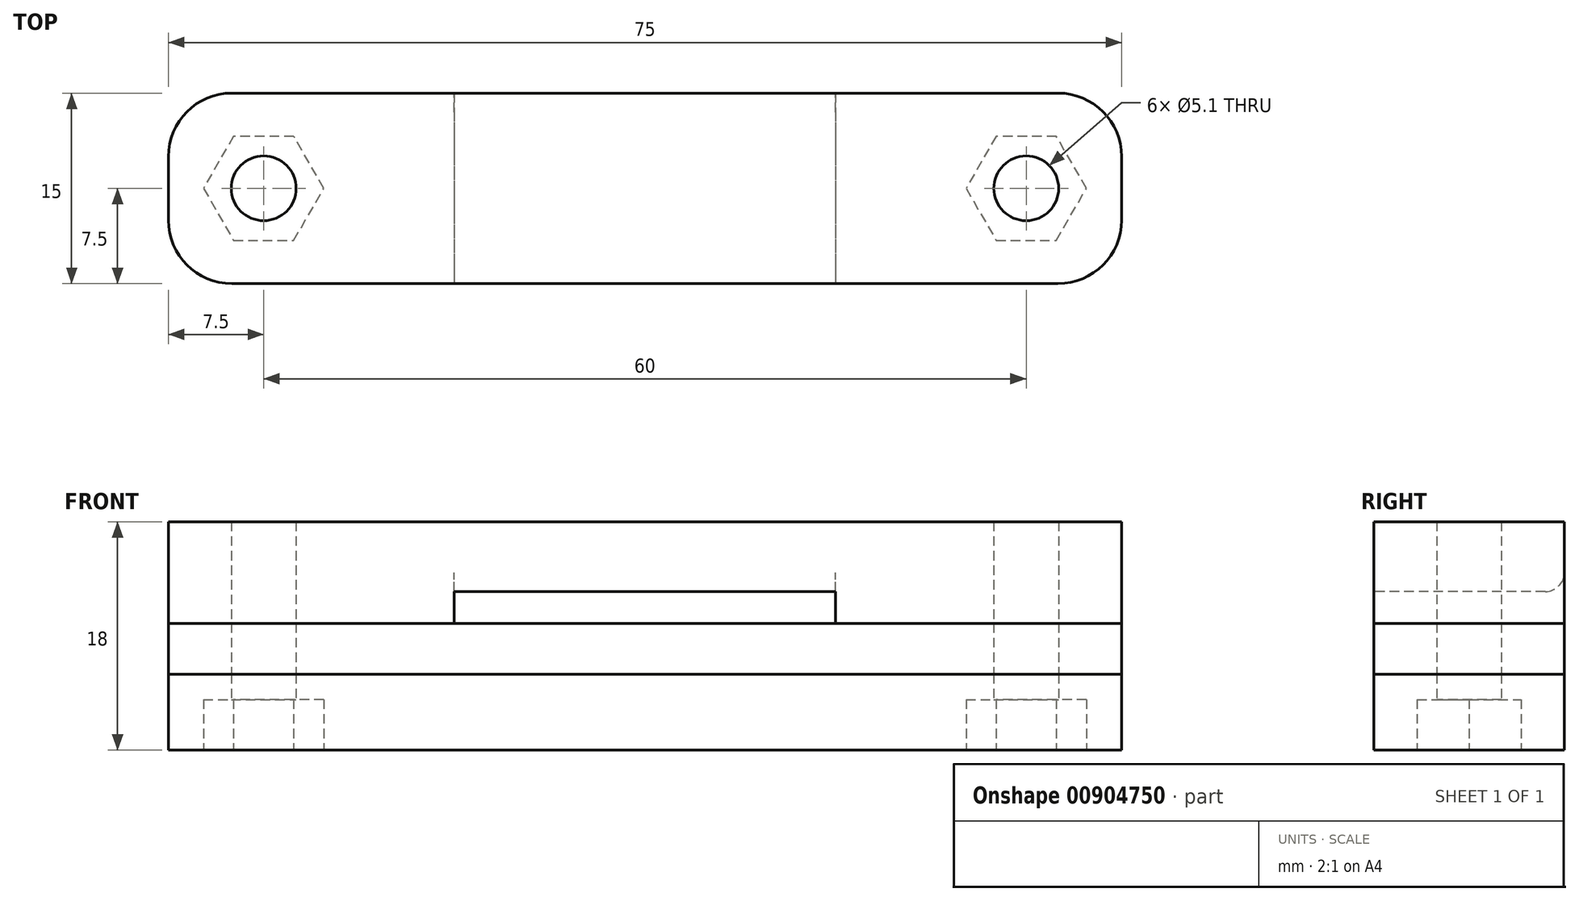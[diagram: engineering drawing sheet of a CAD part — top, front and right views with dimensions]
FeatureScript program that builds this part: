
annotation { "Feature Type Name" : "Feature", "Feature Type Description" : "" }
export const myFeature = defineFeature(function(context is Context, id is Id, definition is map)
    precondition{}
    {
        {
            var Q0;
            Q0=qCreatedBy(makeId("Top.planeOp"),FACE);
            var sketch = newSketch(context, id + "F0", { "sketchPlane" : qUnion([Q0])});
            skLineSegment(sketch, "E0.bottom", {"start": v(32.5, -7.5) * mm, "end": v(-32.5, -7.5) * mm});
            skLineSegment(sketch, "E0.top", {"start": v(32.5, 7.5) * mm, "end": v(-32.5, 7.5) * mm});
            skLineSegment(sketch, "E0.left", {"start": v(37.5, -2.5) * mm, "end": v(37.5, 2.5) * mm});
            skLineSegment(sketch, "E0.right", {"start": v(-37.5, -2.5) * mm, "end": v(-37.5, 2.5) * mm});
            skPoint(sketch, "E0.middle", {"position": v(0, 0) * mm});
            skLineSegment(sketch, "E1", {"start": v(-26.98, 0) * mm, "end": v(-37.5, 0) * mm, "construction": true});
            skLineSegment(sketch, "E2", {"start": v(-37.5, 0) * mm, "end": v(37.5, 0) * mm, "construction": true});
            skCircle(sketch, "E3", {"center": v(-30, 0) * mm, "radius": 2.55 * mm});
            skCircle(sketch, "E4", {"center": v(30, 0) * mm, "radius": 2.55 * mm});
            skLineSegment(sketch, "E5.bottom", {"start": v(25, -3.26) * mm, "end": v(-25, -3.26) * mm, "construction": true});
            skLineSegment(sketch, "E5.top", {"start": v(25, 3.26) * mm, "end": v(-25, 3.26) * mm, "construction": true});
            skLineSegment(sketch, "E5.left", {"start": v(25, -3.26) * mm, "end": v(25, 3.26) * mm, "construction": true});
            skLineSegment(sketch, "E5.right", {"start": v(-25, -3.26) * mm, "end": v(-25, 3.26) * mm, "construction": true});
            skPoint(sketch, "E6.visualSharp", {"position": v(-37.5, 7.5) * mm});
            skArc(sketch, "E6.filletArc", {"start": v(-32.5, 7.5) * mm, "mid": v(-36.04, 6.04) * mm, "end": v(-37.5, 2.5) * mm});
            skPoint(sketch, "E7.visualSharp", {"position": v(-37.5, -7.5) * mm});
            skArc(sketch, "E7.filletArc", {"start": v(-37.5, -2.5) * mm, "mid": v(-36.04, -6.04) * mm, "end": v(-32.5, -7.5) * mm});
            skPoint(sketch, "E8.visualSharp", {"position": v(37.5, -7.5) * mm});
            skArc(sketch, "E8.filletArc", {"start": v(32.5, -7.5) * mm, "mid": v(36.04, -6.04) * mm, "end": v(37.5, -2.5) * mm});
            skPoint(sketch, "E9.visualSharp", {"position": v(37.5, 7.5) * mm});
            skArc(sketch, "E9.filletArc", {"start": v(37.5, 2.5) * mm, "mid": v(36.04, 6.04) * mm, "end": v(32.5, 7.5) * mm});
            skSolve(sketch);
        }
        {
            var Q0;
            Q0=makeQuery(id+"F0.imprint","IMPRINT",FACE,{"disambiguationData":[TD([[makeQuery(id+"F0.imprint","IMPRINT",EDGE,{"derivedFrom":sQuery(id+"F0.wireOp",EDGE,"E0.bottom")}),-1.0]])]});
            extrude(context, id + "F1", {"entities" : qUnion([Q0]), "depth" : 6 * mm, "offsetDistance" : 25 * mm});
        }
        {
            var Q0;
            Q0=makeQuery(id+"F1.opExtrude","CAP_FACE",FACE,{"disambiguationData":[OSD([sQuery(id+"F0.wireOp",EDGE,"E0.bottom"),sQuery(id+"F0.wireOp",EDGE,"E0.top"),sQuery(id+"F0.wireOp",EDGE,"E0.left"),sQuery(id+"F0.wireOp",EDGE,"E0.right"),sQuery(id+"F0.wireOp",EDGE,"E3"),sQuery(id+"F0.wireOp",EDGE,"E4"),sQuery(id+"F0.wireOp",EDGE,"E6.filletArc"),sQuery(id+"F0.wireOp",EDGE,"E7.filletArc"),sQuery(id+"F0.wireOp",EDGE,"E8.filletArc"),sQuery(id+"F0.wireOp",EDGE,"E9.filletArc")])],"isStart":true});
            var sketch = newSketch(context, id + "F2", { "sketchPlane" : qUnion([Q0])});
            skCircle(sketch, "E10.cCircle", {"center": v(-30, 0) * mm, "radius": 4.1 * mm, "construction": true});
            skLineSegment(sketch, "E10.0", {"start": v(-27.63, -4.1) * mm, "end": v(-32.37, -4.1) * mm});
            skLineSegment(sketch, "E10.1", {"start": v(-32.37, -4.1) * mm, "end": v(-34.73, 0) * mm});
            skLineSegment(sketch, "E10.2", {"start": v(-34.73, 0) * mm, "end": v(-32.37, 4.1) * mm});
            skLineSegment(sketch, "E10.3", {"start": v(-32.37, 4.1) * mm, "end": v(-27.63, 4.1) * mm});
            skLineSegment(sketch, "E10.4", {"start": v(-27.63, 4.1) * mm, "end": v(-25.27, 0) * mm});
            skLineSegment(sketch, "E10.5", {"start": v(-25.27, 0) * mm, "end": v(-27.63, -4.1) * mm});
            skPoint(sketch, "E10.0.midPoint", {"position": v(-30, -4.1) * mm});
            skCircle(sketch, "E11.cCircle", {"center": v(30, 0) * mm, "radius": 4.1 * mm, "construction": true});
            skLineSegment(sketch, "E11.0", {"start": v(32.37, -4.1) * mm, "end": v(27.63, -4.1) * mm});
            skLineSegment(sketch, "E11.1", {"start": v(27.63, -4.1) * mm, "end": v(25.27, 0) * mm});
            skLineSegment(sketch, "E11.2", {"start": v(25.27, 0) * mm, "end": v(27.63, 4.1) * mm});
            skLineSegment(sketch, "E11.3", {"start": v(27.63, 4.1) * mm, "end": v(32.37, 4.1) * mm});
            skLineSegment(sketch, "E11.4", {"start": v(32.37, 4.1) * mm, "end": v(34.73, 0) * mm});
            skLineSegment(sketch, "E11.5", {"start": v(34.73, 0) * mm, "end": v(32.37, -4.1) * mm});
            skPoint(sketch, "E11.0.midPoint", {"position": v(30, -4.1) * mm});
            skSolve(sketch);
        }
        {
            var Q0;
            Q0 = qSketchRegion(id + "F2", true);
            extrude(context, id + "F3", {"entities" : qUnion([Q0]), "operationType" : NewBodyOperationType.REMOVE, "oppositeDirection" : true, "depth" : 4 * mm, "offsetDistance" : 25 * mm});
        }
        {
            var Q0;
            Q0=makeQuery(id+"F1.opExtrude","CAP_FACE",FACE,{"disambiguationData":[OSD([sQuery(id+"F0.wireOp",EDGE,"E0.bottom"),sQuery(id+"F0.wireOp",EDGE,"E0.top"),sQuery(id+"F0.wireOp",EDGE,"E0.left"),sQuery(id+"F0.wireOp",EDGE,"E0.right"),sQuery(id+"F0.wireOp",EDGE,"E3"),sQuery(id+"F0.wireOp",EDGE,"E4"),sQuery(id+"F0.wireOp",EDGE,"E6.filletArc"),sQuery(id+"F0.wireOp",EDGE,"E7.filletArc"),sQuery(id+"F0.wireOp",EDGE,"E8.filletArc"),sQuery(id+"F0.wireOp",EDGE,"E9.filletArc")])],"isStart":false});
            var sketch = newSketch(context, id + "F4", { "sketchPlane" : qUnion([Q0])});
            skLineSegment(sketch, "E12.0", {"start": v(32.5, -7.5) * mm, "end": v(-32.5, -7.5) * mm});
            skLineSegment(sketch, "E13.0", {"start": v(32.5, 7.5) * mm, "end": v(-32.5, 7.5) * mm});
            skArc(sketch, "E14.0", {"start": v(37.5, 2.5) * mm, "mid": v(36.04, 6.04) * mm, "end": v(32.5, 7.5) * mm});
            skLineSegment(sketch, "E15.0", {"start": v(37.5, -2.5) * mm, "end": v(37.5, 2.5) * mm});
            skArc(sketch, "E16.0", {"start": v(32.5, -7.5) * mm, "mid": v(36.04, -6.04) * mm, "end": v(37.5, -2.5) * mm});
            skArc(sketch, "E17.0", {"start": v(-37.5, -2.5) * mm, "mid": v(-36.04, -6.04) * mm, "end": v(-32.5, -7.5) * mm});
            skPoint(sketch, "E18.0", {"position": v(-37.5, 2.5) * mm});
            skArc(sketch, "E19.0", {"start": v(-32.5, 7.5) * mm, "mid": v(-36.04, 6.04) * mm, "end": v(-37.5, 2.5) * mm});
            skLineSegment(sketch, "E20.0", {"start": v(-37.5, -2.5) * mm, "end": v(-37.5, 2.5) * mm});
            skCircle(sketch, "E21.0", {"center": v(-30, 0) * mm, "radius": 2.55 * mm});
            skCircle(sketch, "E22.0", {"center": v(30, 0) * mm, "radius": 2.55 * mm});
            skSolve(sketch);
        }
        {
            var Q0;
            Q0 = qSketchRegion(id + "F4", true);
            extrude(context, id + "F5", {"entities" : qUnion([Q0]), "depth" : 4 * mm, "offsetDistance" : 25 * mm});
        }
        {
            var Q0;
            Q0=makeQuery(id+"F5.opExtrude","CAP_FACE",FACE,{"disambiguationData":[OSD([sQuery(id+"F4.wireOp",EDGE,"E12.0"),sQuery(id+"F4.wireOp",EDGE,"E13.0"),sQuery(id+"F4.wireOp",EDGE,"E14.0"),sQuery(id+"F4.wireOp",EDGE,"E15.0"),sQuery(id+"F4.wireOp",EDGE,"E16.0"),sQuery(id+"F4.wireOp",EDGE,"E17.0"),sQuery(id+"F4.wireOp",EDGE,"E19.0"),sQuery(id+"F4.wireOp",EDGE,"E20.0"),sQuery(id+"F4.wireOp",EDGE,"E21.0"),sQuery(id+"F4.wireOp",EDGE,"E22.0")])],"isStart":false});
            var sketch = newSketch(context, id + "F6", { "sketchPlane" : qUnion([Q0])});
            skLineSegment(sketch, "E23.0", {"start": v(32.5, 7.5) * mm, "end": v(-32.5, 7.5) * mm});
            skArc(sketch, "E24.0", {"start": v(37.5, 2.5) * mm, "mid": v(36.04, 6.04) * mm, "end": v(32.5, 7.5) * mm});
            skPoint(sketch, "E25.0", {"position": v(37.5, -2.5) * mm});
            skLineSegment(sketch, "E26.0", {"start": v(37.5, -2.5) * mm, "end": v(37.5, 2.5) * mm});
            skArc(sketch, "E27.0", {"start": v(32.5, -7.5) * mm, "mid": v(36.04, -6.04) * mm, "end": v(37.5, -2.5) * mm});
            skLineSegment(sketch, "E28.0", {"start": v(32.5, -7.5) * mm, "end": v(-32.5, -7.5) * mm});
            skCircle(sketch, "E29.0", {"center": v(30, 0) * mm, "radius": 2.55 * mm});
            skArc(sketch, "E30.0", {"start": v(-32.5, 7.5) * mm, "mid": v(-36.04, 6.04) * mm, "end": v(-37.5, 2.5) * mm});
            skLineSegment(sketch, "E31.0", {"start": v(-37.5, -2.5) * mm, "end": v(-37.5, 2.5) * mm});
            skArc(sketch, "E32.0", {"start": v(-37.5, -2.5) * mm, "mid": v(-36.04, -6.04) * mm, "end": v(-32.5, -7.5) * mm});
            skCircle(sketch, "E33.0", {"center": v(-30, 0) * mm, "radius": 2.55 * mm});
            skSolve(sketch);
        }
        {
            var Q0;
            Q0 = qSketchRegion(id + "F6", true);
            extrude(context, id + "F7", {"entities" : qUnion([Q0]), "depth" : 8 * mm, "offsetDistance" : 25 * mm});
        }
        {
            var Q0;
            Q0=makeQuery(id+"F7.opExtrude","SWEPT_FACE",FACE,{"disambiguationData":[OSD([sQuery(id+"F6.wireOp",EDGE,"E28.0")])]});
            var sketch = newSketch(context, id + "F8", { "sketchPlane" : qUnion([Q0])});
            skLineSegment(sketch, "E34.bottom", {"start": v(15, 7.5) * mm, "end": v(-15, 7.5) * mm});
            skLineSegment(sketch, "E34.top", {"start": v(15, 12.5) * mm, "end": v(-15, 12.5) * mm});
            skLineSegment(sketch, "E34.left", {"start": v(15, 7.5) * mm, "end": v(15, 12.5) * mm});
            skLineSegment(sketch, "E34.right", {"start": v(-15, 7.5) * mm, "end": v(-15, 12.5) * mm});
            skPoint(sketch, "E34.middle", {"position": v(0, 10) * mm});
            skSolve(sketch);
        }
        {
            var Q0;
            {var subQ0=sQuery(id+"F8.wireOp",EDGE,"E34.top");Q0=makeQuery(id+"F8.imprint","IMPRINT",FACE,{"disambiguationData":[TD([[makeQuery(id+"F8.imprint","IMPRINT",EDGE,{"derivedFrom":subQ0}),1.0]])]});}
            extrude(context, id + "F9", {"entities" : qUnion([Q0]), "operationType" : NewBodyOperationType.REMOVE, "endBound" : BoundingType.THROUGH_ALL, "oppositeDirection" : true, "depth" : 25 * mm, "offsetDistance" : 25 * mm});
        }
        {
            var Q0;
            Q0=makeQuery(id+"F9.boolean.opBoolean","INTERSECT",EDGE,{"derivedFrom":[makeQuery(id+"F7.opExtrude","SWEPT_FACE",FACE,{"disambiguationData":[OSD([sQuery(id+"F6.wireOp",EDGE,"E23.0")])]}),makeQuery(id+"F9.opExtrude","SWEPT_FACE",FACE,{"disambiguationData":[OSD([sQuery(id+"F8.wireOp",EDGE,"E34.top")])]})]});
            var Q1;
            Q1=makeQuery(id+"F9.boolean.opBoolean","COPY",EDGE,{"derivedFrom":makeQuery(id+"F9.opExtrude","CAP_EDGE",EDGE,{"disambiguationData":[OSD([sQuery(id+"F8.wireOp",EDGE,"E34.top")])],"isStart":true})});
            fillet(context, id + "F10", {"entities" : qUnion([Q0, Q1]), "radius" : 1.5 * mm, "tangentPropagation" : true, "allowEdgeOverflow" : false});
        }
    });
